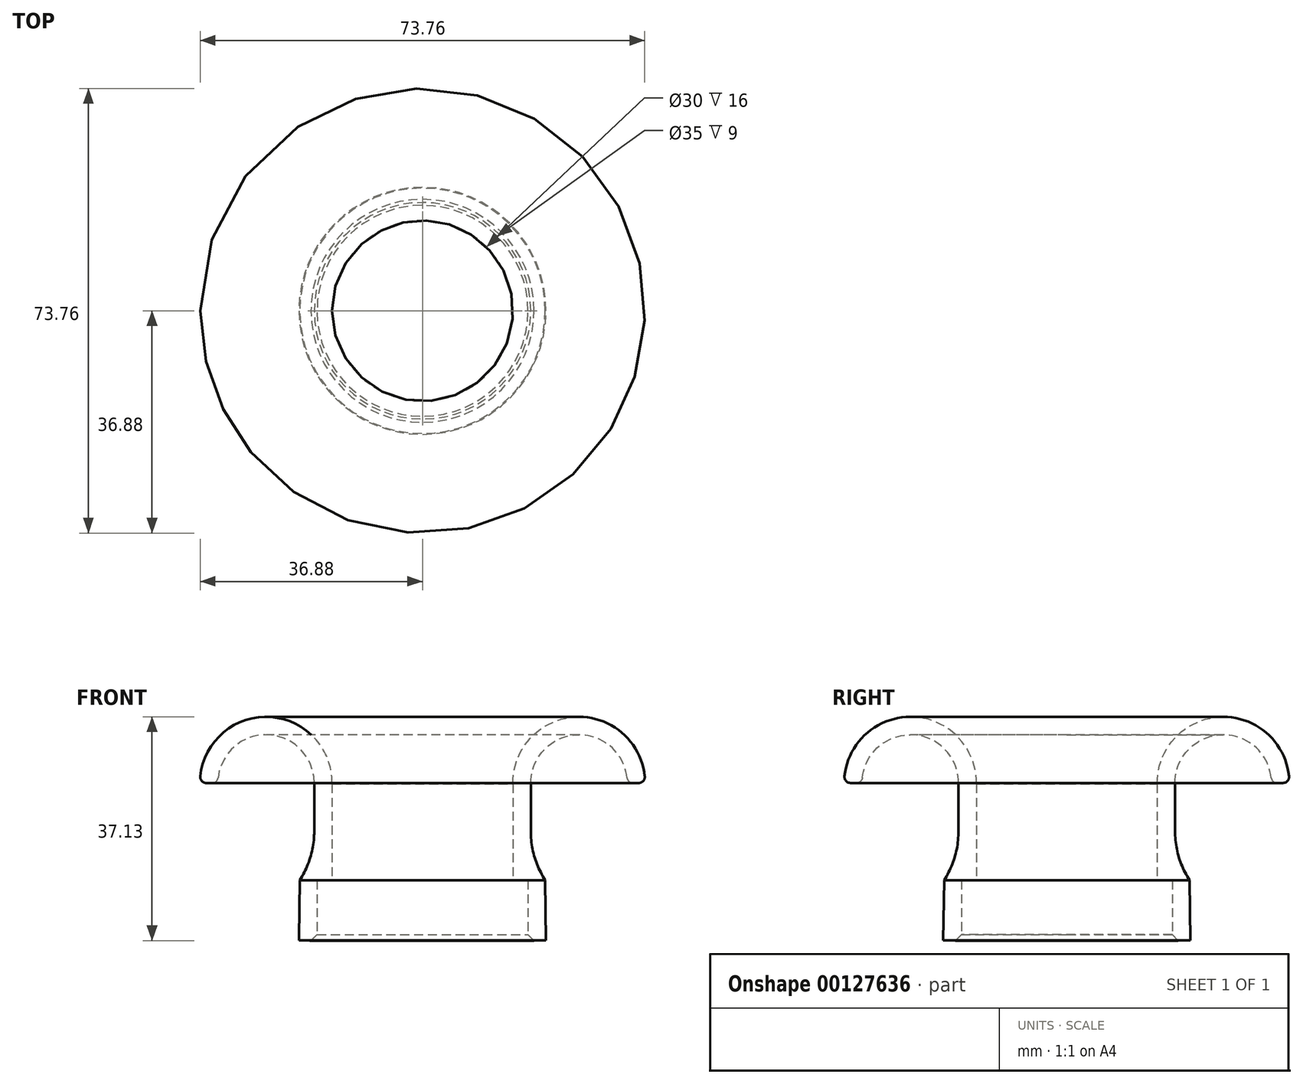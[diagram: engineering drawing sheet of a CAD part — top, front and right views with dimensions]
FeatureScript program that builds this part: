
annotation { "Feature Type Name" : "Feature", "Feature Type Description" : "" }
export const myFeature = defineFeature(function(context is Context, id is Id, definition is map)
    precondition{}
    {
        {
            var Q0;
            Q0=qCreatedBy(makeId("Front.planeOp"),FACE);
            var sketch = newSketch(context, id + "F0", { "sketchPlane" : qUnion([Q0])});
            skPoint(sketch, "E0.second.point", {"position": v(77.54, 19) * mm});
            skPoint(sketch, "E0.third.point", {"position": v(37.2, 56.24) * mm});
            skArc(sketch, "E1", {"start": v(21.93, 19.17) * mm, "mid": v(10.88, 30.14) * mm, "end": v(0, 19) * mm});
            skLineSegment(sketch, "E2", {"start": v(2.03, 0) * mm, "end": v(0, 0) * mm});
            skLineSegment(sketch, "E3", {"start": v(0, 0) * mm, "end": v(2.03, 0) * mm});
            skPoint(sketch, "E4.orphan", {"position": v(4.05, 0) * mm});
            skLineSegment(sketch, "E5", {"start": v(0, 0) * mm, "end": v(-15, 0) * mm});
            skLineSegment(sketch, "E6", {"start": v(-15, 0) * mm, "end": v(-15, 56.91) * mm});
            skArc(sketch, "E7", {"start": v(18.97, 19.17) * mm, "mid": v(10.97, 27.17) * mm, "end": v(2.97, 19.17) * mm});
            skCircle(sketch, "E8", {"center": v(9.55, 20) * mm, "radius": 0.83 * mm});
            skLineSegment(sketch, "E9", {"start": v(18.97, 19.17) * mm, "end": v(21.93, 19.17) * mm});
            skPoint(sketch, "E10.end.orphan", {"position": v(4.05, 10.65) * mm});
            skPoint(sketch, "E11.visualSharp", {"position": v(7.56, 0) * mm});
            skLineSegment(sketch, "E12", {"start": v(0, 19) * mm, "end": v(0, 3) * mm});
            skLineSegment(sketch, "E13", {"start": v(2.97, 19.17) * mm, "end": v(2.97, 11.17) * mm});
            skLineSegment(sketch, "E14", {"start": v(0, 3) * mm, "end": v(2.5, 3) * mm});
            skLineSegment(sketch, "E15", {"start": v(2.5, 3) * mm, "end": v(2.5, -7) * mm});
            skLineSegment(sketch, "E16", {"start": v(2.5, -7) * mm, "end": v(5.5, -6.96) * mm});
            skLineSegment(sketch, "E17", {"start": v(5.5, -6.96) * mm, "end": v(5.36, 3.04) * mm});
            skArc(sketch, "E18", {"start": v(2.97, 11.17) * mm, "mid": v(3.58, 6.93) * mm, "end": v(5.36, 3.04) * mm});
            skSolve(sketch);
        }
        {
            var Q0;
            {var subQ0=sQuery(id+"F0.wireOp",EDGE,"E1");Q0=makeQuery(id+"F0.imprint","IMPRINT",FACE,{"disambiguationData":[TD([[makeQuery(id+"F0.imprint","IMPRINT",EDGE,{"derivedFrom":subQ0}),1.0]])]});}
            var Q1;
            {var subQ2=sQuery(id+"F0.wireOp",EDGE,"zA0rpZqB-saLa-AZ3N-ox9s-bJx4H0fNbBDQ");Q1=makeQuery(id+"F0.imprint","IMPRINT",FACE,{"disambiguationData":[TD([[makeQuery(id+"F0.imprint","IMPRINT",EDGE,{"derivedFrom":subQ2}),-1.0]])]});}
            var Q2;
            Q2=sQuery(id+"F0.wireOp",EDGE,"E6");
            revolve(context, id + "F1", {"entities" : qUnion([Q0, Q1]), "axis" : qUnion([Q2]), "revolveType" : RevolveType.FULL});
        }
        {
            var Q0;
            Q0=makeQuery(id+"F1.opRevolve","SWEPT_EDGE",EDGE,{"disambiguationData":[OSD([sQuery(id+"F0.wireOp",EDGE,"E1"),sQuery(id+"F0.wireOp",EDGE,"E9")])]});
            var Q1;
            Q1=makeQuery(id+"F1.opRevolve","SWEPT_EDGE",EDGE,{"disambiguationData":[OSD([sQuery(id+"F0.wireOp",EDGE,"E7"),sQuery(id+"F0.wireOp",EDGE,"E9")])]});
            fillet(context, id + "F2", {"entities" : qUnion([Q0, Q1]), "radius" : 1 * mm, "tangentPropagation" : true, "allowEdgeOverflow" : false});
        }
        {
            var Q0;
            Q0=makeQuery(id+"F1.opRevolve","SWEPT_EDGE",EDGE,{"disambiguationData":[OSD([sQuery(id+"F0.wireOp",EDGE,"E15"),sQuery(id+"F0.wireOp",EDGE,"E16")])]});
            chamfer(context, id + "F3", {"entities" : qUnion([Q0]), "width" : 1 * mm, "tangentPropagation" : true});
        }
    });
